# Revit family: Grab Rail_Metlam_30 Deg_Wrap Around_Left
name_source: partatom
category: Specialty Equipment
revit_build: Autodesk Revit 2016 (Build: 20170117_1200(x64)
units: mm (PartAtom-declared; Revit-internal decimal feet)

## family parameters
Always vertical = Yes
Cut with Voids When Loaded = No
OmniClass Number = 23.40.20.21.47
OmniClass Title = Bath Grab Bars
Part Type = Normal
Room Calculation Point = Yes
Round Connector Dimension = Use Diameter
Shared = No
Work Plane-Based = No

## types (1)
- 1522w x 1116d x 382h (MLR113MKII)
    Depth = 1116 mm
    Description = 30° Flush Mount Wrap Around Grab Rail LH
    Height = 382 mm
    Manufacturer = Metlam
    Manufacturer_Depth = 1100 mm
    Manufacturer_Height = 350 mm
    Manufacturer_Spec Code = MLR113MKII
    Manufacturer_URL__Product Specific = https://www.metlam.com.au
    Manufacturer_Width = 1506 mm  [stored 4.94094 ft]
    Material_ANZRS = z_Metlam_Metal_Stainless Steel_Satin
    Model = MLR113MKII
    Type Comments = Grab Rails
    URL = http://www.metlam.com.au
    Width = 1522 mm

note: [stored X ft] marks values corroborated as IEEE doubles in the binary element streams (Revit-internal decimal feet)

## geometry (parser evidence)
native form markers: Sweep x2
no freeform markers — native parametric forms only
